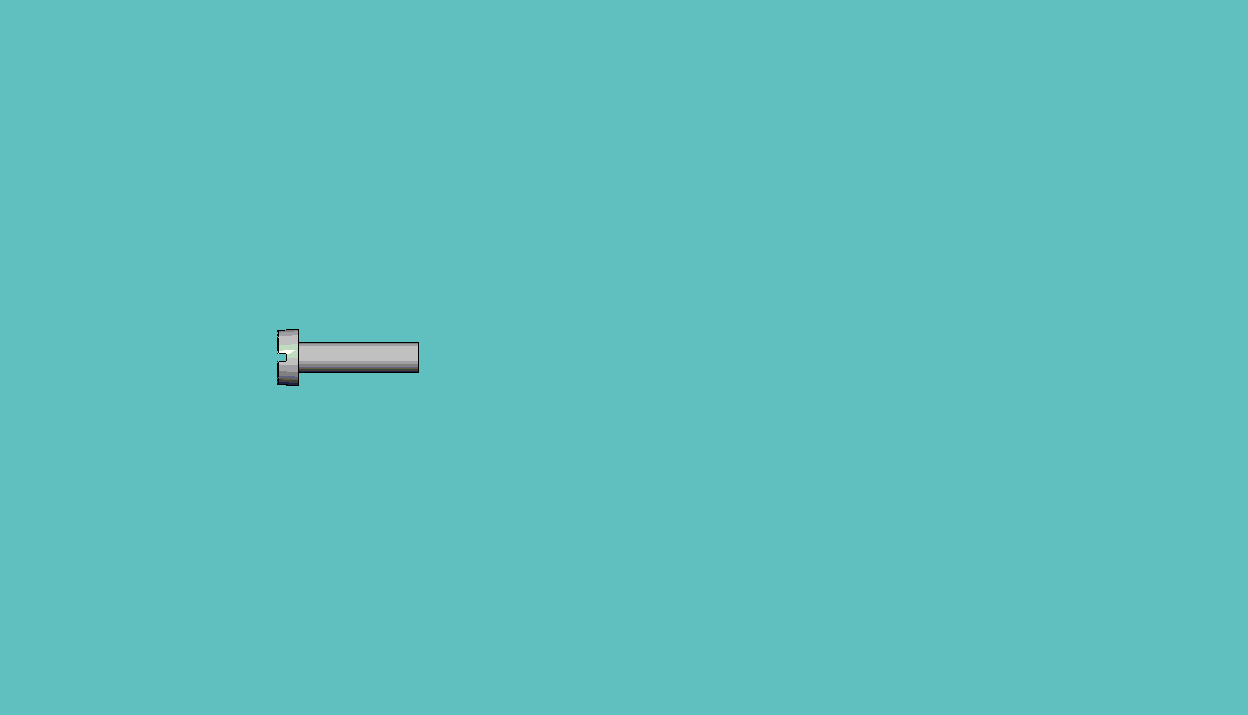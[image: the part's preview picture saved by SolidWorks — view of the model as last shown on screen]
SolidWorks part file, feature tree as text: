
SOLIDWORKS PART (.sldprt)
format: sldprt  version: not decoded by parser v0  size: 190,976 bytes
history: native  units: mm
features: plane x3, sketch x3, fillet x2, material x1, revolve x1, thread x1, cut_extrude x1, cut_revolve x1, pattern_linear x1 (+8 scaffold rows collapsed)
feature tree (22):
  scaffold x8  (default folders/planes/origin — collapsed)
  material  "Matériau <non spécifié>"
  plane  "Plane1"
  plane  "Plane2"
  plane  "Plane3"
  sketch  "BodySke"  dims[c1.Head_fillet_rad=3.6322mm c1.D1=~7.099516mm c1.Head_ang=85.0deg c1.Oval_ht=2.3876mm c1.Head_ht=6.1976mm c1.Diameter=9.525mm c1.Length=76.2mm c1.Head_dia=20.0152mm c2.Head_dia=15.3924mm c2.Head_ht=8.509mm c2.Length=8.0mm c2.Head_side_ht=6.1722mm c3.Head_ht=1.4mm c3.Head_dia=18.4912mm c3.Advance=0.4mm c3.Thread_nom=8.0mm c3.Thread_lim=36.5125mm c4.Head_dia=3.8mm c4.D2=152.4mm c4.Head_side_angle=5.0deg c4.Diameter=2.0mm]
  revolve  "Base-Revolve"  [1 undecoded]
  thread  "ThreadCosmetic"  Diameter=7.2mm Thread_length=7.2mm Thread_minor=1.548mm  [1 undecoded]
  fillet  "Fillet1"  Radius=0.1mm Head_dia=3.8mm Diameter=2mm
  fillet  "Fillet2"  Radius=0.1mm
  sketch  "Sketch2"  dims[D1=3.8mm Slot_width=0.5mm D2=1.9mm D3=0.25mm]
  cut_extrude  "Slot"  Depth=0.6mm Slot_depth=0.6mm
  sketch  "ThdSchSke"  dims[c1.Thread_minor=~1.03886mm c1.Diameter=~1.413535mm c1.Start=~0.988134mm c1.D4=~4.446753mm c1.Vee=60.0deg c2.Thread_minor=~1.03886mm c2.Start=~2.540025mm c2.D1=~0.108159mm c2.D2=~0.108159mm c3.D1=~0.216319mm c3.SideAngle=55.0deg c3.D2=~0.216319mm c3.VeeAngle=70.0deg c3.Thread_minor=1.548mm c3.Overcut=2.5mm c3.Diameter=2.0mm c3.D6=~8.326268mm c4.D1=~8.326268mm c5.D1=90.0deg c5.Start=11.1125mm c6.Start=~44.450025mm c7.Start=2.2mm]
  cut_revolve  "ThreadSchematic"  Angle=360deg
  pattern_linear  "ThdSchPat"  Count1=19 Count2=1 Spacing1=0.4mm Spacing2=50mm Num_threads=19 Advance=0.4mm ConfigurationName=0mm CopiedFlag=1 PartNumberID=0mm
decode coverage: 9 of 10 modeling features carry decoded parameters
note: ~ marks probable driven/reference dimensions
note: 2 parameter values undecoded
note: suppression state not decoded; provenance and decode notes live in map.json
